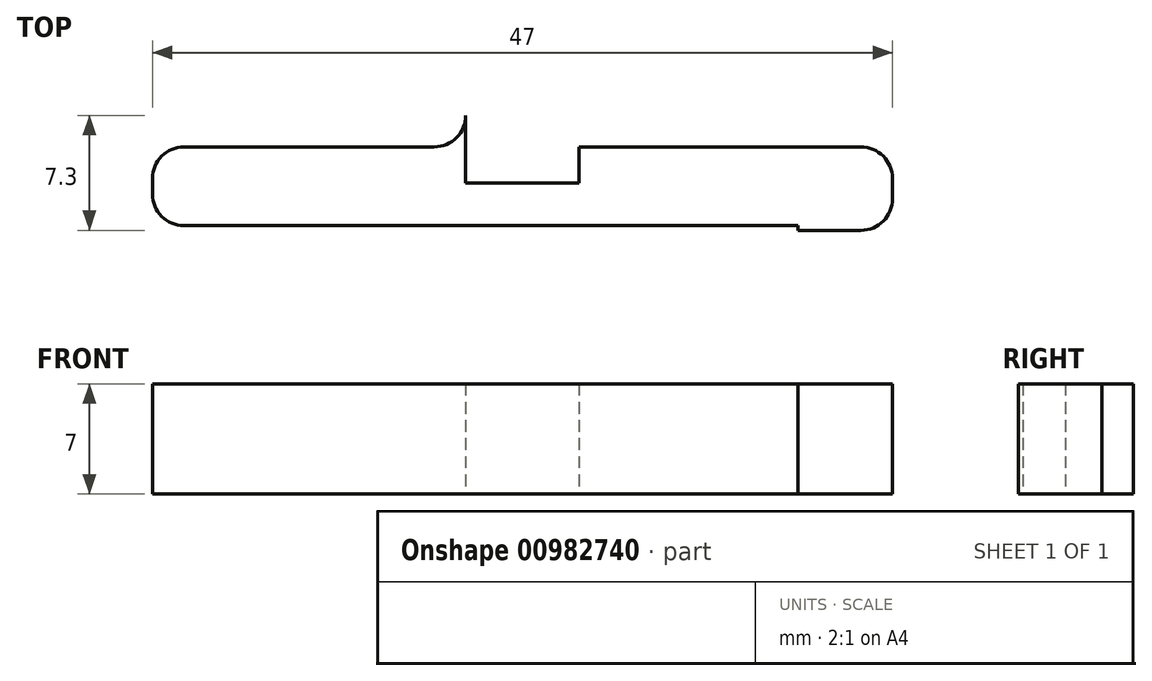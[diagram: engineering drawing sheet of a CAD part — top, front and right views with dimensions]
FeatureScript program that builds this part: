
annotation { "Feature Type Name" : "Feature", "Feature Type Description" : "" }
export const myFeature = defineFeature(function(context is Context, id is Id, definition is map)
    precondition{}
    {
        {
            var Q0;
            Q0=qCreatedBy(makeId("Top.planeOp"),FACE);
            var sketch = newSketch(context, id + "F0", { "sketchPlane" : qUnion([Q0])});
            skLineSegment(sketch, "E0.bottom", {"start": v(-23.5, 5) * mm, "end": v(23.5, 5) * mm});
            skLineSegment(sketch, "E0.top", {"start": v(-23.5, 0) * mm, "end": v(23.5, 0) * mm});
            skLineSegment(sketch, "E0.left", {"start": v(-23.5, 5) * mm, "end": v(-23.5, 0) * mm});
            skLineSegment(sketch, "E0.right", {"start": v(23.5, 5) * mm, "end": v(23.5, 0) * mm});
            skPoint(sketch, "E0.middle", {"position": v(0, 2.5) * mm});
            skLineSegment(sketch, "E1.bottom", {"start": v(3.6, 2.7) * mm, "end": v(-3.6, 2.7) * mm});
            skLineSegment(sketch, "E1.top", {"start": v(3.6, 5) * mm, "end": v(-3.6, 5) * mm});
            skLineSegment(sketch, "E1.left", {"start": v(3.6, 2.7) * mm, "end": v(3.6, 5) * mm});
            skLineSegment(sketch, "E1.right", {"start": v(-3.6, 2.7) * mm, "end": v(-3.6, 5) * mm});
            skPoint(sketch, "E1.middle", {"position": v(0, 3.85) * mm});
            skLineSegment(sketch, "E2", {"start": v(-3.6, 5) * mm, "end": v(-3.6, 7) * mm});
            skArc(sketch, "E3", {"start": v(-5.6, 5) * mm, "mid": v(-4.19, 5.59) * mm, "end": v(-3.6, 7) * mm});
            skArc(sketch, "E4.MirrorCS", {"start": v(5.6, 5) * mm, "mid": v(4.19, 5.59) * mm, "end": v(3.6, 7) * mm});
            skLineSegment(sketch, "E5.MirrorCS", {"start": v(3.6, 5) * mm, "end": v(3.6, 7) * mm});
            skLineSegment(sketch, "E6.bottom", {"start": v(-23.5, 0) * mm, "end": v(-17.5, 0) * mm});
            skLineSegment(sketch, "E6.top", {"start": v(-23.5, -0.3) * mm, "end": v(-17.5, -0.3) * mm});
            skLineSegment(sketch, "E6.left", {"start": v(-23.5, 0) * mm, "end": v(-23.5, -0.3) * mm});
            skLineSegment(sketch, "E6.right", {"start": v(-17.5, 0) * mm, "end": v(-17.5, -0.3) * mm});
            skLineSegment(sketch, "E7.MirrorCS", {"start": v(23.5, -0.3) * mm, "end": v(17.5, -0.3) * mm});
            skLineSegment(sketch, "E8.MirrorCS", {"start": v(23.5, 0) * mm, "end": v(23.5, -0.3) * mm});
            skLineSegment(sketch, "E9.MirrorCS", {"start": v(17.5, 0) * mm, "end": v(17.5, -0.3) * mm});
            skLineSegment(sketch, "E10.MirrorCS", {"start": v(23.5, 0) * mm, "end": v(17.5, 0) * mm});
            skSolve(sketch);
        }
        {
            var Q0;
            {var subQ0=sQuery(id+"F0.wireOp",EDGE,"E2");Q0=makeQuery(id+"F0.imprint","IMPRINT",FACE,{"disambiguationData":[TD([[makeQuery(id+"F0.imprint","IMPRINT",EDGE,{"derivedFrom":subQ0}),1.0]])]});}
            var Q1;
            {var subQ2=sQuery(id+"F0.wireOp",EDGE,"E4.MirrorCS");Q1=makeQuery(id+"F0.imprint","IMPRINT",FACE,{"disambiguationData":[TD([[makeQuery(id+"F0.imprint","IMPRINT",EDGE,{"derivedFrom":subQ2}),1.0]])]});}
            var Q2;
            Q2=makeQuery(id+"F0.imprint","IMPRINT",FACE,{"disambiguationData":[TD([[makeQuery(id+"F0.imprint","IMPRINT",EDGE,{"derivedFrom":sQuery(id+"F0.wireOp",EDGE,"E6.bottom")}),-1.0]])]});
            var Q3;
            Q3=makeQuery(id+"F0.imprint","IMPRINT",FACE,{"disambiguationData":[TD([[makeQuery(id+"F0.imprint","IMPRINT",EDGE,{"derivedFrom":sQuery(id+"F0.wireOp",EDGE,"E0.top")}),1.0]])]});
            var Q4;
            Q4=makeQuery(id+"F0.imprint","IMPRINT",FACE,{"disambiguationData":[TD([[makeQuery(id+"F0.imprint","IMPRINT",EDGE,{"derivedFrom":sQuery(id+"F0.wireOp",EDGE,"E7.MirrorCS")}),-1.0]])]});
            extrude(context, id + "F1", {"entities" : qUnion([Q0, Q1, Q2, Q3, Q4]), "depth" : 7 * mm, "offsetDistance" : 25 * mm});
        }
        {
            var Q0;
            Q0=makeQuery(id+"F1.opExtrude","SWEPT_EDGE",EDGE,{"disambiguationData":[OSD([sQuery(id+"F0.wireOp",EDGE,"E0.bottom"),sQuery(id+"F0.wireOp",EDGE,"E0.left")])]});
            var Q1;
            Q1=makeQuery(id+"F1.opExtrude","SWEPT_EDGE",EDGE,{"disambiguationData":[OSD([sQuery(id+"F0.wireOp",EDGE,"E0.bottom"),sQuery(id+"F0.wireOp",EDGE,"E0.right")])]});
            var Q2;
            Q2=makeQuery(id+"F1.opExtrude","SWEPT_EDGE",EDGE,{"disambiguationData":[OSD([sQuery(id+"F0.wireOp",EDGE,"E6.top"),sQuery(id+"F0.wireOp",EDGE,"E6.left")])]});
            var Q3;
            Q3=makeQuery(id+"F1.opExtrude","SWEPT_EDGE",EDGE,{"disambiguationData":[OSD([sQuery(id+"F0.wireOp",EDGE,"E7.MirrorCS"),sQuery(id+"F0.wireOp",EDGE,"E8.MirrorCS")])]});
            fillet(context, id + "F2", {"entities" : qUnion([Q0, Q1, Q2, Q3]), "radius" : 2 * mm, "tangentPropagation" : true, "allowEdgeOverflow" : false});
        }
    });
